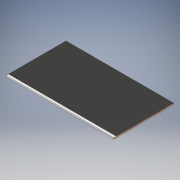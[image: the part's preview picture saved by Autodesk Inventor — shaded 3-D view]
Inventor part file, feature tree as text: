
AUTODESK INVENTOR PART (.ipt)
format: ipt  version: 2017 (Build 210142000, 142)  size: 102,912 bytes
history: native  units: in
note: dims shown in document units (in); Inventor stores cm internally (conversion verified against a paired STEP export)
features: extrude x2, sketch x2
ambient origin geometry x8: Origin, YZ Plane, XZ Plane, XY Plane, X Axis, Y Axis, Z Axis, Center Point
bodies: Solid1 (feature_tree)
feature tree (4):
  extrude  "Extrusion1"  Depth=25.0in
  extrude  "Extrusion2"  Depth=1.0in
  sketch  "Sketch1"  dims[d0=45.0in d1=25.0in]
  sketch  "Sketch2"  dims[d2=0.5in d3=0.0in d4=1.0in d5=0.001in d6=0.0in]
